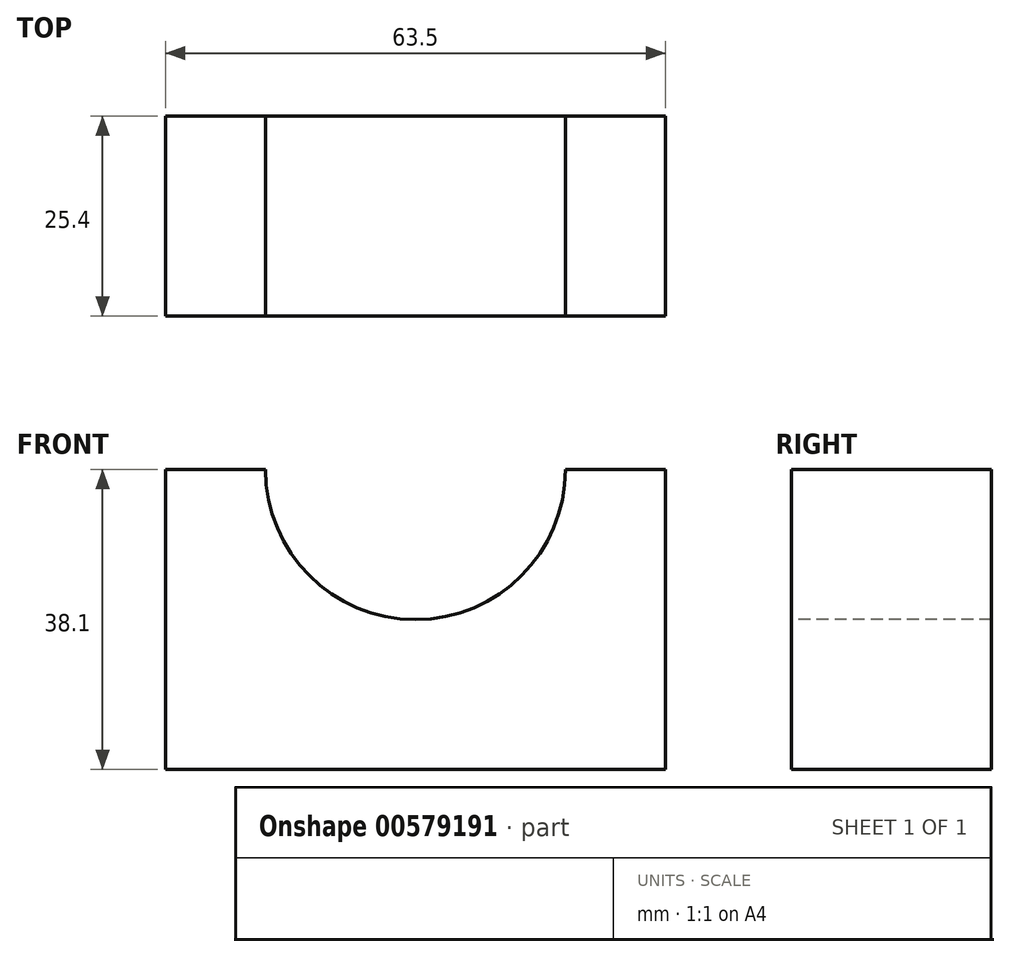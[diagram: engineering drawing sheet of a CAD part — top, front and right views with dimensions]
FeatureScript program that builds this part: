
annotation { "Feature Type Name" : "Feature", "Feature Type Description" : "" }
export const myFeature = defineFeature(function(context is Context, id is Id, definition is map)
    precondition{}
    {
        {
            var Q0;
            Q0=qCreatedBy(makeId("Front.planeOp"),FACE);
            var sketch = newSketch(context, id + "F0", { "sketchPlane" : qUnion([Q0])});
            skLineSegment(sketch, "E0", {"start": v(-91.02, 50.84) * mm, "end": v(-91.02, 12.74) * mm});
            skLineSegment(sketch, "E1", {"start": v(-91.02, 12.74) * mm, "end": v(-27.52, 12.74) * mm});
            skLineSegment(sketch, "E2", {"start": v(-27.52, 12.74) * mm, "end": v(-27.52, 50.84) * mm});
            skLineSegment(sketch, "E3", {"start": v(-27.52, 50.84) * mm, "end": v(-91.02, 50.84) * mm});
            skSolve(sketch);
        }
        {
            var Q0;
            Q0 = qSketchRegion(id + "F0", true);
            extrude(context, id + "F1", {"entities" : qUnion([Q0]), "depth" : 25.4 * mm, "offsetDistance" : 25.4 * mm});
        }
        {
            var Q0;
            Q0=makeQuery(id+"F1.opExtrude","CAP_FACE",FACE,{"disambiguationData":[OSD([sQuery(id+"F0.wireOp",EDGE,"E0"),sQuery(id+"F0.wireOp",EDGE,"E1"),sQuery(id+"F0.wireOp",EDGE,"E2"),sQuery(id+"F0.wireOp",EDGE,"E3")])],"isStart":false});
            var sketch = newSketch(context, id + "F2", { "sketchPlane" : qUnion([Q0])});
            skArc(sketch, "E4", {"start": v(-78.32, 50.84) * mm, "mid": v(-59.27, 31.79) * mm, "end": v(-40.22, 50.84) * mm});
            skSolve(sketch);
        }
        {
            var Q0;
            {var subQ0=sQuery(id+"F2.wireOp",EDGE,"E4");Q0=makeQuery(id+"F2.imprint","IMPRINT",FACE,{"disambiguationData":[TD([[makeQuery(id+"F2.imprint","IMPRINT",EDGE,{"derivedFrom":subQ0}),1.0]])]});}
            extrude(context, id + "F3", {"entities" : qUnion([Q0]), "operationType" : NewBodyOperationType.REMOVE, "oppositeDirection" : true, "depth" : 25.4 * mm, "offsetDistance" : 25.4 * mm});
        }
    });
